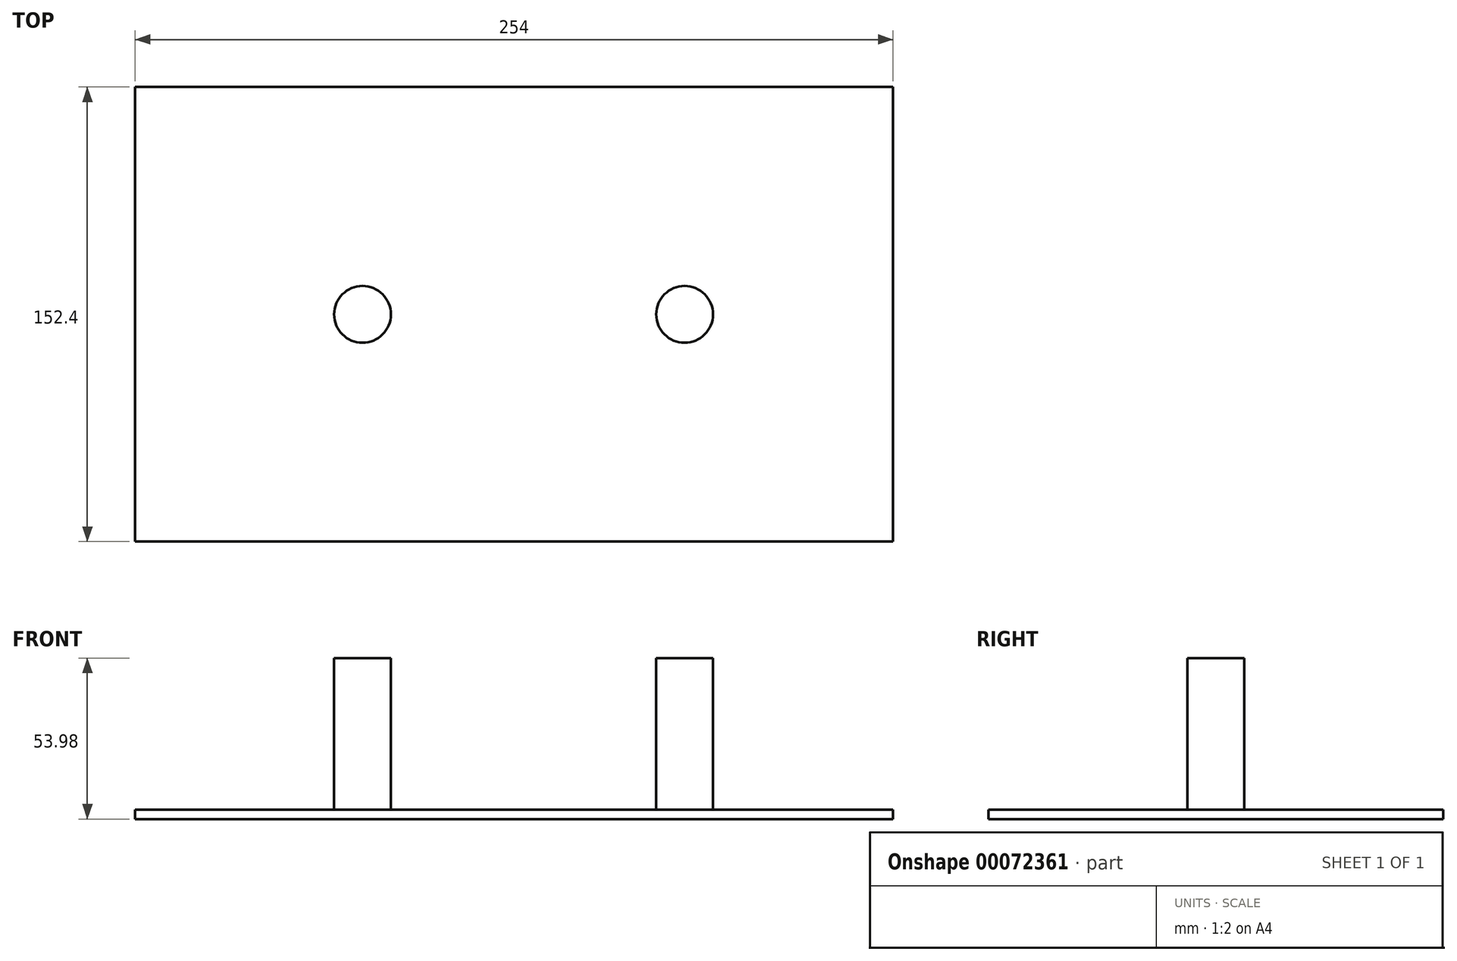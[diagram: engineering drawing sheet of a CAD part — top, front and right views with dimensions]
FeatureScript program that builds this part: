
annotation { "Feature Type Name" : "Feature", "Feature Type Description" : "" }
export const myFeature = defineFeature(function(context is Context, id is Id, definition is map)
    precondition{}
    {
        {
            var Q0;
            Q0=qCreatedBy(makeId("Top.planeOp"),FACE);
            var sketch = newSketch(context, id + "F0", { "sketchPlane" : qUnion([Q0])});
            skLineSegment(sketch, "E0.rect.bottom", {"start": v(127, 76.2) * mm, "end": v(-127, 76.2) * mm});
            skLineSegment(sketch, "E0.rect.top", {"start": v(127, -76.2) * mm, "end": v(-127, -76.2) * mm});
            skLineSegment(sketch, "E0.rect.left", {"start": v(127, 76.2) * mm, "end": v(127, -76.2) * mm});
            skLineSegment(sketch, "E0.rect.right", {"start": v(-127, 76.2) * mm, "end": v(-127, -76.2) * mm});
            skPoint(sketch, "E0.rect.middle", {"position": v(0, 0) * mm});
            skSolve(sketch);
        }
        {
            var Q0;
            Q0=makeQuery(id+"F0.imprint","IMPRINT",FACE,{"disambiguationData":[TD([[makeQuery(id+"F0.imprint","IMPRINT",EDGE,{"derivedFrom":sQuery(id+"F0.wireOp",EDGE,"E0.rect.bottom")}),1.0]])]});
            extrude(context, id + "F1", {"entities" : qUnion([Q0]), "depth" : 3.17 * mm});
        }
        {
            var Q0;
            Q0=makeQuery(id+"F1.opExtrude","CAP_FACE",FACE,{"disambiguationData":[OSD([sQuery(id+"F0.wireOp",EDGE,"E0.rect.bottom"),sQuery(id+"F0.wireOp",EDGE,"E0.rect.top"),sQuery(id+"F0.wireOp",EDGE,"E0.rect.left"),sQuery(id+"F0.wireOp",EDGE,"E0.rect.right")])],"isStart":false});
            var sketch = newSketch(context, id + "F2", { "sketchPlane" : qUnion([Q0])});
            skCircle(sketch, "E1", {"center": v(-50.8, 0) * mm, "radius": 9.53 * mm});
            skCircle(sketch, "E2", {"center": v(57.15, 0) * mm, "radius": 9.53 * mm});
            skSolve(sketch);
        }
        {
            var Q0;
            Q0=makeQuery(id+"F2.imprint","IMPRINT",FACE,{"disambiguationData":[TD([[makeQuery(id+"F2.imprint","IMPRINT",EDGE,{"derivedFrom":sQuery(id+"F2.wireOp",EDGE,"E1")}),1.0]])]});
            var Q1;
            Q1=makeQuery(id+"F2.imprint","IMPRINT",FACE,{"disambiguationData":[TD([[makeQuery(id+"F2.imprint","IMPRINT",EDGE,{"derivedFrom":sQuery(id+"F2.wireOp",EDGE,"E2")}),1.0]])]});
            extrude(context, id + "F3", {"entities" : qUnion([Q0, Q1]), "operationType" : NewBodyOperationType.ADD, "depth" : 50.8 * mm});
        }
    });
